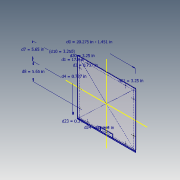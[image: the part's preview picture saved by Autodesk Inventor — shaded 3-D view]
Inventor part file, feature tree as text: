
AUTODESK INVENTOR PART (.ipt)
format: ipt  version: 2020.3 (Build 243373000, 373)  size: 146,432 bytes
history: native  units: in
note: dims shown in document units (in); Inventor stores cm internally (conversion verified against a paired STEP export)
features: fillet x3, sketch x1, extrude x1, hole x1
ambient origin geometry x8: Origin, YZ Plane, XZ Plane, XY Plane, X Axis, Y Axis, Z Axis, Center Point
bodies: Solid1 (feature_tree)
feature tree (6):
  sketch  "Sketch1"  dims[d0=18.824in d1=17.8in d3=0.737in d4=0.737in d7=5.65in d8=5.65in d10=3.25in d11=0.177in d12=0.0in d13=0.325in d14=0.75in d15=0.375in d16=0.25in d17=0.5635in d18=1.0in d19=0.8108in d20=3.25in d21=3.25in d22=0.375in d23=0.3in d24=1.378in d25=4.0in d26=0.375in d27=0.125in]
  extrude  "Extrusion1"  Depth=0.125in
  hole  "Hole1"  [1 undecoded]
  fillet  "Fillet1"  Radius=0.737in
  fillet  "Fillet2"  Radius=5.65in
  fillet  "Fillet3"  Radius=5.65in
note: 1 required parameter value undecoded (feature->parameter linkage not recoverable at this tier; creation-order binding heuristic only, values carry confidence <= 0.55)
